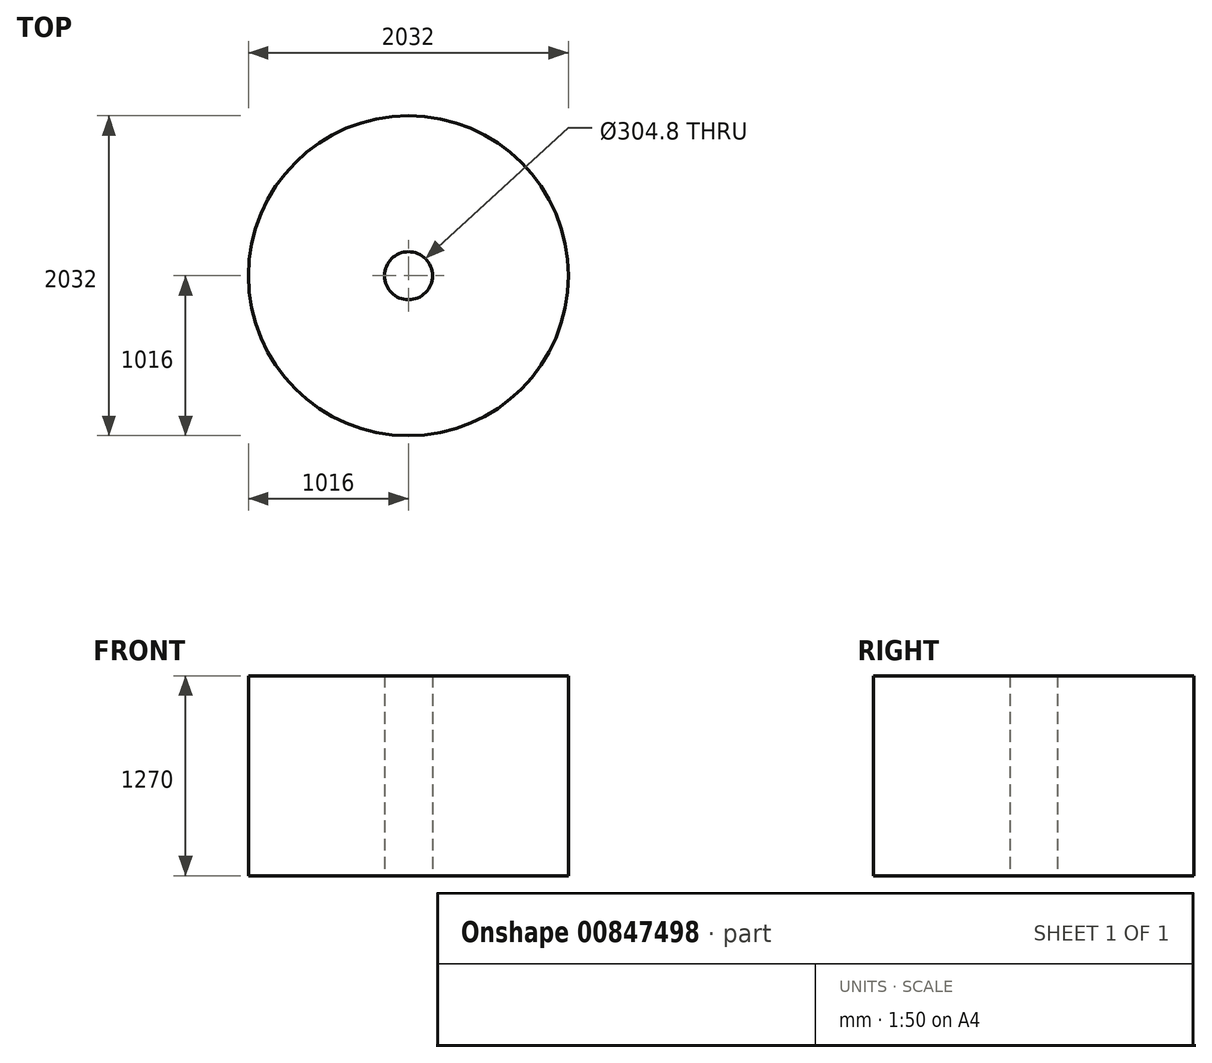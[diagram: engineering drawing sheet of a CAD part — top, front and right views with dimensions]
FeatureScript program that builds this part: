
annotation { "Feature Type Name" : "Feature", "Feature Type Description" : "" }
export const myFeature = defineFeature(function(context is Context, id is Id, definition is map)
    precondition{}
    {
        {
            var Q0;
            Q0=qCreatedBy(makeId("Top.planeOp"),FACE);
            var sketch = newSketch(context, id + "F0", { "sketchPlane" : qUnion([Q0])});
            skCircle(sketch, "E0", {"center": v(0, 0) * mm, "radius": 1016 * mm});
            skCircle(sketch, "E1", {"center": v(0, 0) * mm, "radius": 152.4 * mm});
            skSolve(sketch);
        }
        {
            var Q0;
            Q0=makeQuery(id+"F0.imprint","IMPRINT",FACE,{"disambiguationData":[TD([[makeQuery(id+"F0.imprint","IMPRINT",EDGE,{"derivedFrom":sQuery(id+"F0.wireOp",EDGE,"E0")}),1.0]])]});
            extrude(context, id + "F1", {"entities" : qUnion([Q0]), "depth" : 1270 * mm, "offsetDistance" : 25.4 * mm});
        }
    });
